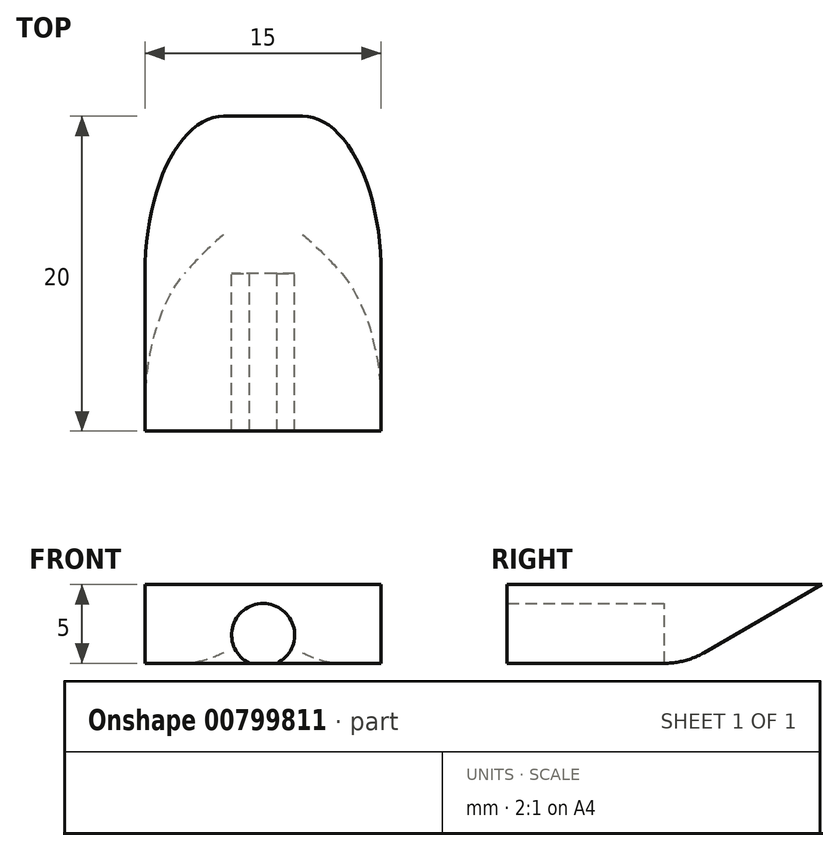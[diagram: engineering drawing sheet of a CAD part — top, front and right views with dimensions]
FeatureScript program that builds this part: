
annotation { "Feature Type Name" : "Feature", "Feature Type Description" : "" }
export const myFeature = defineFeature(function(context is Context, id is Id, definition is map)
    precondition{}
    {
        {
            var Q0;
            Q0=qCreatedBy(makeId("Front.planeOp"),FACE);
            var sketch = newSketch(context, id + "F0", { "sketchPlane" : qUnion([Q0])});
            skLineSegment(sketch, "E0.bottom", {"start": v(7.5, -2.5) * mm, "end": v(0.87, -2.5) * mm});
            skLineSegment(sketch, "E0.top", {"start": v(7.5, 2.5) * mm, "end": v(-7.5, 2.5) * mm});
            skLineSegment(sketch, "E0.left", {"start": v(7.5, -2.5) * mm, "end": v(7.5, 2.5) * mm});
            skLineSegment(sketch, "E0.right", {"start": v(-7.5, -2.5) * mm, "end": v(-7.5, 2.5) * mm});
            skPoint(sketch, "E0.middle", {"position": v(0, 0) * mm});
            skArc(sketch, "E1", {"start": v(0.87, -2.5) * mm, "mid": v(0, 1.3) * mm, "end": v(-0.87, -2.5) * mm});
            skPoint(sketch, "E1.centerSnap0", {"position": v(0, -2.5) * mm});
            skLineSegment(sketch, "E2.trimOffspring", {"start": v(-0.87, -2.5) * mm, "end": v(-7.5, -2.5) * mm});
            skSolve(sketch);
        }
        {
            var Q0;
            Q0=makeQuery(id+"F0.imprint","IMPRINT",FACE,{"disambiguationData":[TD([[makeQuery(id+"F0.imprint","IMPRINT",EDGE,{"derivedFrom":sQuery(id+"F0.wireOp",EDGE,"E0.bottom")}),-1.0]])]});
            extrude(context, id + "F1", {"entities" : qUnion([Q0]), "depth" : 10 * mm, "offsetDistance" : 25 * mm});
        }
        {
            var Q0;
            Q0=makeQuery(id+"F1.opExtrude","CAP_FACE",FACE,{"disambiguationData":[OSD([sQuery(id+"F0.wireOp",EDGE,"E0.bottom"),sQuery(id+"F0.wireOp",EDGE,"E0.top"),sQuery(id+"F0.wireOp",EDGE,"E0.left"),sQuery(id+"F0.wireOp",EDGE,"E0.right"),sQuery(id+"F0.wireOp",EDGE,"E1"),sQuery(id+"F0.wireOp",EDGE,"E2.trimOffspring")])],"isStart":true});
            var sketch = newSketch(context, id + "F2", { "sketchPlane" : qUnion([Q0])});
            skLineSegment(sketch, "E3.0", {"start": v(-7.5, 2.5) * mm, "end": v(7.5, 2.5) * mm});
            skPoint(sketch, "E4.0", {"position": v(-7.5, 0) * mm});
            skLineSegment(sketch, "E5.0", {"start": v(-7.5, -2.5) * mm, "end": v(-7.5, 2.5) * mm});
            skLineSegment(sketch, "E6.0", {"start": v(-7.5, -2.5) * mm, "end": v(-0.87, -2.5) * mm});
            skLineSegment(sketch, "E7.0", {"start": v(0.87, -2.5) * mm, "end": v(7.5, -2.5) * mm});
            skLineSegment(sketch, "E8.0", {"start": v(7.5, -2.5) * mm, "end": v(7.5, 2.5) * mm});
            skLineSegment(sketch, "E9", {"start": v(-0.87, -2.5) * mm, "end": v(0.87, -2.5) * mm});
            skSolve(sketch);
        }
        {
            var Q0;
            Q0=makeQuery(id+"F2.imprint","IMPRINT",FACE,{"disambiguationData":[TD([[makeQuery(id+"F2.imprint","IMPRINT",EDGE,{"derivedFrom":sQuery(id+"F2.wireOp",EDGE,"E9")}),1.0]])]});
            var Q1;
            Q1=makeQuery(id+"F2.imprint","IMPRINT",FACE,{"disambiguationData":[TD([[makeQuery(id+"F2.imprint","IMPRINT",EDGE,{"derivedFrom":sQuery(id+"F2.wireOp",EDGE,"E3.0")}),-1.0]])]});
            extrude(context, id + "F3", {"entities" : qUnion([Q0, Q1]), "operationType" : NewBodyOperationType.ADD, "depth" : 10 * mm, "offsetDistance" : 25 * mm});
        }
        {
            var Q0;
            Q0=makeQuery(id+"F3.opExtrude","CAP_EDGE",EDGE,{"disambiguationData":[OSD([sQuery(id+"F2.wireOp",EDGE,"E6.0"),sQuery(id+"F2.wireOp",EDGE,"E7.0"),sQuery(id+"F2.wireOp",EDGE,"E9")])],"isStart":false});
            chamfer(context, id + "F4", {"entities" : qUnion([Q0]), "chamferType" : ChamferType.OFFSET_ANGLE, "width" : 5 * mm, "oppositeDirection" : false, "angle" : 60 * degree, "tangentPropagation" : true});
        }
        {
            var Q0;
            {var subQ0=sQuery(id+"F2.wireOp",EDGE,"E9");var subQ1=sQuery(id+"F2.wireOp",EDGE,"E7.0");var subQ2=sQuery(id+"F2.wireOp",EDGE,"E6.0");Q0=makeQuery(id+"F4.opChamfer","BLEND_EDGE",EDGE,{"blendedFrom":[makeQuery(id+"F3.opExtrude","CAP_EDGE",EDGE,{"disambiguationData":[OSD([subQ2,subQ1,subQ0])],"isStart":false}),makeQuery(id+"F3.boolean.opBoolean","MERGE",FACE,{"derivedFrom":[makeQuery(id+"F1.opExtrude","SWEPT_FACE",FACE,{"disambiguationData":[OSD([sQuery(id+"F0.wireOp",EDGE,"E0.bottom")])]}),makeQuery(id+"F1.opExtrude","SWEPT_FACE",FACE,{"disambiguationData":[OSD([sQuery(id+"F0.wireOp",EDGE,"E2.trimOffspring")])]}),makeQuery(id+"F3.opExtrude","SWEPT_FACE",FACE,{"disambiguationData":[OSD([subQ2,subQ1,subQ0])]})]})],"blendedInto":[makeQuery(id+"F3.boolean.opBoolean","MERGE",FACE,{"derivedFrom":[makeQuery(id+"F1.opExtrude","SWEPT_FACE",FACE,{"disambiguationData":[OSD([sQuery(id+"F0.wireOp",EDGE,"E0.bottom")])]}),makeQuery(id+"F1.opExtrude","SWEPT_FACE",FACE,{"disambiguationData":[OSD([sQuery(id+"F0.wireOp",EDGE,"E2.trimOffspring")])]}),makeQuery(id+"F3.opExtrude","SWEPT_FACE",FACE,{"disambiguationData":[OSD([subQ2,subQ1,subQ0])]})]})]});}
            var Q1;
            Q1=makeQuery(id+"F4.opChamfer","BLEND_EDGE",EDGE,{"blendedFrom":[makeQuery(id+"F3.opExtrude","CAP_EDGE",EDGE,{"disambiguationData":[OSD([sQuery(id+"F2.wireOp",EDGE,"E6.0"),sQuery(id+"F2.wireOp",EDGE,"E7.0"),sQuery(id+"F2.wireOp",EDGE,"E9")])],"isStart":false}),makeQuery(id+"F3.boolean.opBoolean","MERGE",FACE,{"derivedFrom":[makeQuery(id+"F1.opExtrude","SWEPT_FACE",FACE,{"disambiguationData":[OSD([sQuery(id+"F0.wireOp",EDGE,"E0.left")])]}),makeQuery(id+"F3.opExtrude","SWEPT_FACE",FACE,{"disambiguationData":[OSD([sQuery(id+"F2.wireOp",EDGE,"E5.0")])]})]})],"blendedInto":[makeQuery(id+"F3.boolean.opBoolean","MERGE",FACE,{"derivedFrom":[makeQuery(id+"F1.opExtrude","SWEPT_FACE",FACE,{"disambiguationData":[OSD([sQuery(id+"F0.wireOp",EDGE,"E0.left")])]}),makeQuery(id+"F3.opExtrude","SWEPT_FACE",FACE,{"disambiguationData":[OSD([sQuery(id+"F2.wireOp",EDGE,"E5.0")])]})]})]});
            var Q2;
            Q2=makeQuery(id+"F4.opChamfer","BLEND_EDGE",EDGE,{"blendedFrom":[makeQuery(id+"F3.opExtrude","CAP_EDGE",EDGE,{"disambiguationData":[OSD([sQuery(id+"F2.wireOp",EDGE,"E6.0"),sQuery(id+"F2.wireOp",EDGE,"E7.0"),sQuery(id+"F2.wireOp",EDGE,"E9")])],"isStart":false}),makeQuery(id+"F3.boolean.opBoolean","MERGE",FACE,{"derivedFrom":[makeQuery(id+"F1.opExtrude","SWEPT_FACE",FACE,{"disambiguationData":[OSD([sQuery(id+"F0.wireOp",EDGE,"E0.right")])]}),makeQuery(id+"F3.opExtrude","SWEPT_FACE",FACE,{"disambiguationData":[OSD([sQuery(id+"F2.wireOp",EDGE,"E8.0")])]})]})],"blendedInto":[makeQuery(id+"F3.boolean.opBoolean","MERGE",FACE,{"derivedFrom":[makeQuery(id+"F1.opExtrude","SWEPT_FACE",FACE,{"disambiguationData":[OSD([sQuery(id+"F0.wireOp",EDGE,"E0.right")])]}),makeQuery(id+"F3.opExtrude","SWEPT_FACE",FACE,{"disambiguationData":[OSD([sQuery(id+"F2.wireOp",EDGE,"E8.0")])]})]})]});
            fillet(context, id + "F5", {"entities" : qUnion([Q0, Q1, Q2]), "radius" : 5 * mm, "tangentPropagation" : true, "allowEdgeOverflow" : false});
        }
    });
